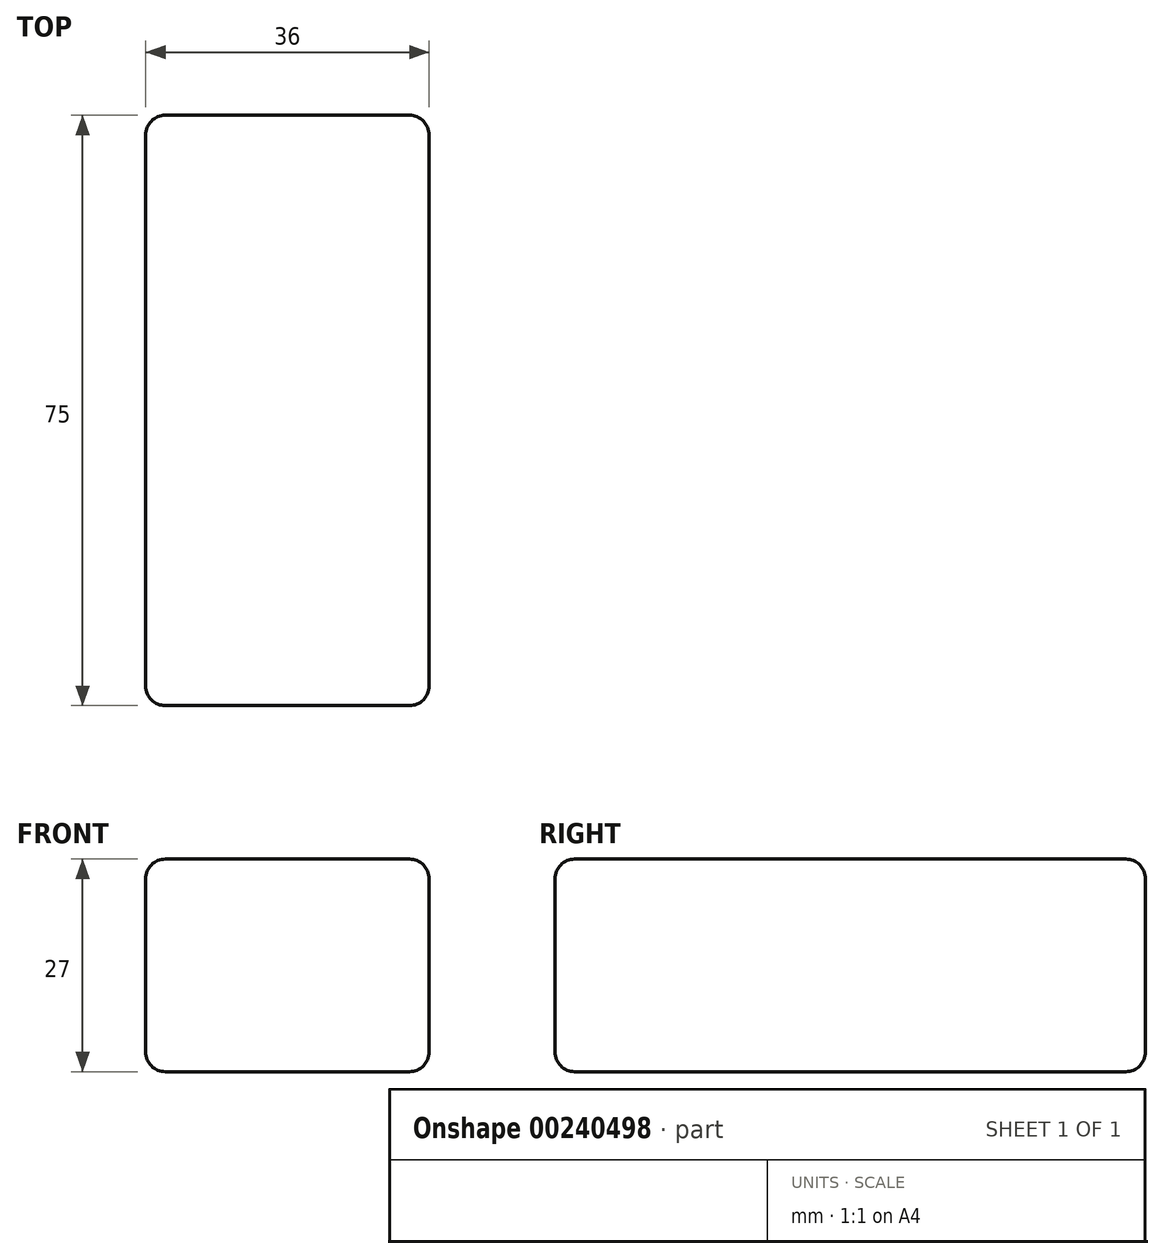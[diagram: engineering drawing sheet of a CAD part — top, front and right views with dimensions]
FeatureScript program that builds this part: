
annotation { "Feature Type Name" : "Feature", "Feature Type Description" : "" }
export const myFeature = defineFeature(function(context is Context, id is Id, definition is map)
    precondition{}
    {
        {
            var Q0;
            Q0=qCreatedBy(makeId("Top.planeOp"),FACE);
            var sketch = newSketch(context, id + "F0", { "sketchPlane" : qUnion([Q0])});
            skLineSegment(sketch, "E0.bottom", {"start": v(18, 37.5) * mm, "end": v(-18, 37.5) * mm});
            skLineSegment(sketch, "E0.top", {"start": v(18, -37.5) * mm, "end": v(-18, -37.5) * mm});
            skLineSegment(sketch, "E0.left", {"start": v(18, 37.5) * mm, "end": v(18, -37.5) * mm});
            skLineSegment(sketch, "E0.right", {"start": v(-18, 37.5) * mm, "end": v(-18, -37.5) * mm});
            skPoint(sketch, "E0.middle", {"position": v(0, 0) * mm});
            skSolve(sketch);
        }
        {
            var Q0;
            Q0=makeQuery(id+"F0.imprint","IMPRINT",FACE,{"disambiguationData":[TD([[makeQuery(id+"F0.imprint","IMPRINT",EDGE,{"derivedFrom":sQuery(id+"F0.wireOp",EDGE,"E0.bottom")}),1.0]])]});
            extrude(context, id + "F1", {"entities" : qUnion([Q0]), "depth" : 27 * mm});
        }
        {
            var Q0;
            Q0=makeQuery(id+"F1.opExtrude","SWEPT_FACE",FACE,{"disambiguationData":[OSD([sQuery(id+"F0.wireOp",EDGE,"E0.left")])]});
            var Q1;
            Q1=makeQuery(id+"F1.opExtrude","SWEPT_FACE",FACE,{"disambiguationData":[OSD([sQuery(id+"F0.wireOp",EDGE,"E0.top")])]});
            var Q2;
            Q2=makeQuery(id+"F1.opExtrude","CAP_FACE",FACE,{"disambiguationData":[OSD([sQuery(id+"F0.wireOp",EDGE,"E0.bottom"),sQuery(id+"F0.wireOp",EDGE,"E0.top"),sQuery(id+"F0.wireOp",EDGE,"E0.left"),sQuery(id+"F0.wireOp",EDGE,"E0.right")])],"isStart":false});
            var Q3;
            Q3=makeQuery(id+"F1.opExtrude","CAP_FACE",FACE,{"disambiguationData":[OSD([sQuery(id+"F0.wireOp",EDGE,"E0.bottom"),sQuery(id+"F0.wireOp",EDGE,"E0.top"),sQuery(id+"F0.wireOp",EDGE,"E0.left"),sQuery(id+"F0.wireOp",EDGE,"E0.right")])],"isStart":true});
            var Q4;
            Q4=makeQuery(id+"F1.opExtrude","SWEPT_FACE",FACE,{"disambiguationData":[OSD([sQuery(id+"F0.wireOp",EDGE,"E0.right")])]});
            fillet(context, id + "F2", {"entities" : qUnion([Q0, Q1, Q2, Q3, Q4]), "radius" : 2.5 * mm, "tangentPropagation" : true, "allowEdgeOverflow" : false});
        }
    });
